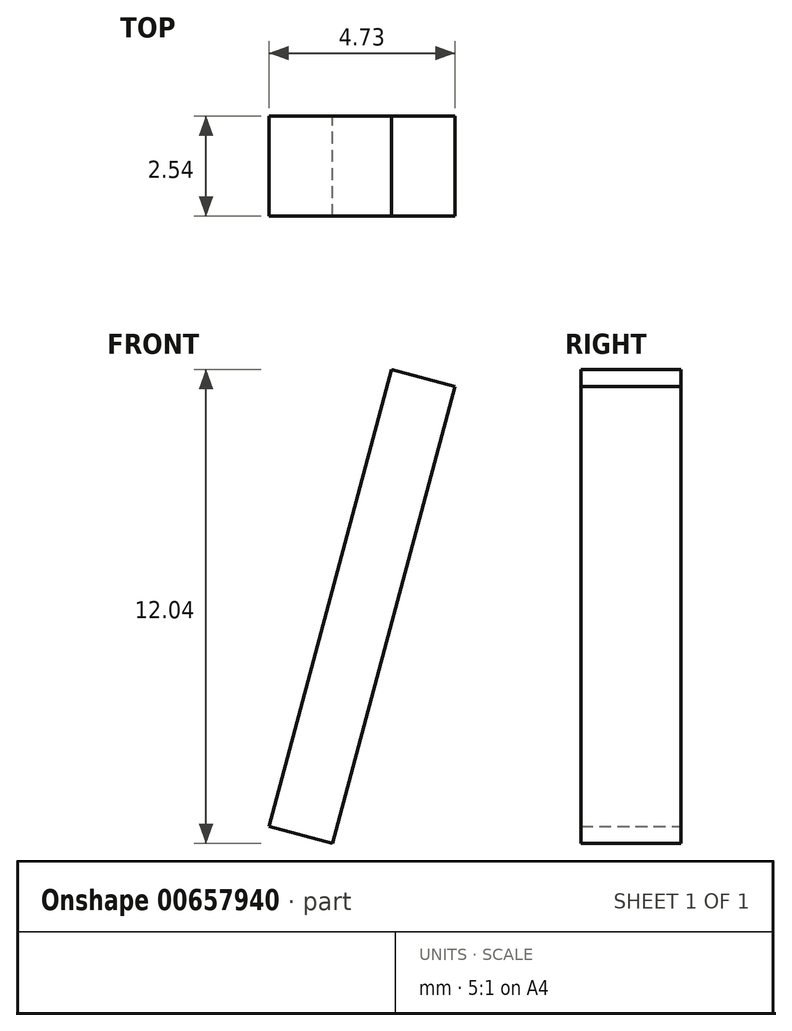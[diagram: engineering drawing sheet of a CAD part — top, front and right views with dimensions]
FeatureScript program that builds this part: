
annotation { "Feature Type Name" : "Feature", "Feature Type Description" : "" }
export const myFeature = defineFeature(function(context is Context, id is Id, definition is map)
    precondition{}
    {
        {
            var Q0;
            Q0=qCreatedBy(makeId("Front.planeOp"),FACE);
            var sketch = newSketch(context, id + "F0", { "sketchPlane" : qUnion([Q0])});
            skLineSegment(sketch, "E0.bottom", {"start": v(0.84, 6) * mm, "end": v(-0.84, 6) * mm});
            skLineSegment(sketch, "E0.top", {"start": v(0.84, -6) * mm, "end": v(-0.84, -6) * mm});
            skLineSegment(sketch, "E0.left", {"start": v(0.84, 6) * mm, "end": v(0.84, -6) * mm});
            skLineSegment(sketch, "E0.right", {"start": v(-0.84, 6) * mm, "end": v(-0.84, -6) * mm});
            skPoint(sketch, "E0.middle", {"position": v(0, 0) * mm});
            skSolve(sketch);
        }
        {
            var Q0;
            Q0 = qSketchRegion(id + "F0", true);
            extrude(context, id + "F1", {"entities" : qUnion([Q0]), "depth" : 2.54 * mm, "offsetDistance" : 25.4 * mm});
        }
        {
            var Q0;
            Q0=makeQuery(id+"F1.opExtrude","SWEPT_BODY",BODY,{"disambiguationData":[OSD([sQuery(id+"F0.wireOp",EDGE,"E0.bottom"),sQuery(id+"F0.wireOp",EDGE,"E0.top"),sQuery(id+"F0.wireOp",EDGE,"E0.left"),sQuery(id+"F0.wireOp",EDGE,"E0.right")])]});
            var Q1;
            Q1=makeQuery(id+"F1.opExtrude","SWEPT_EDGE",EDGE,{"disambiguationData":[OSD([sQuery(id+"F0.wireOp",EDGE,"E0.top"),sQuery(id+"F0.wireOp",EDGE,"E0.left")])]});
            transform(context, id + "F2", {"entities" : qUnion([Q0]), "transformType" : TransformType.ROTATION, "transformAxis" : qUnion([Q1]), "angle" : 15 * degree, "makeCopy" : false});
        }
    });
